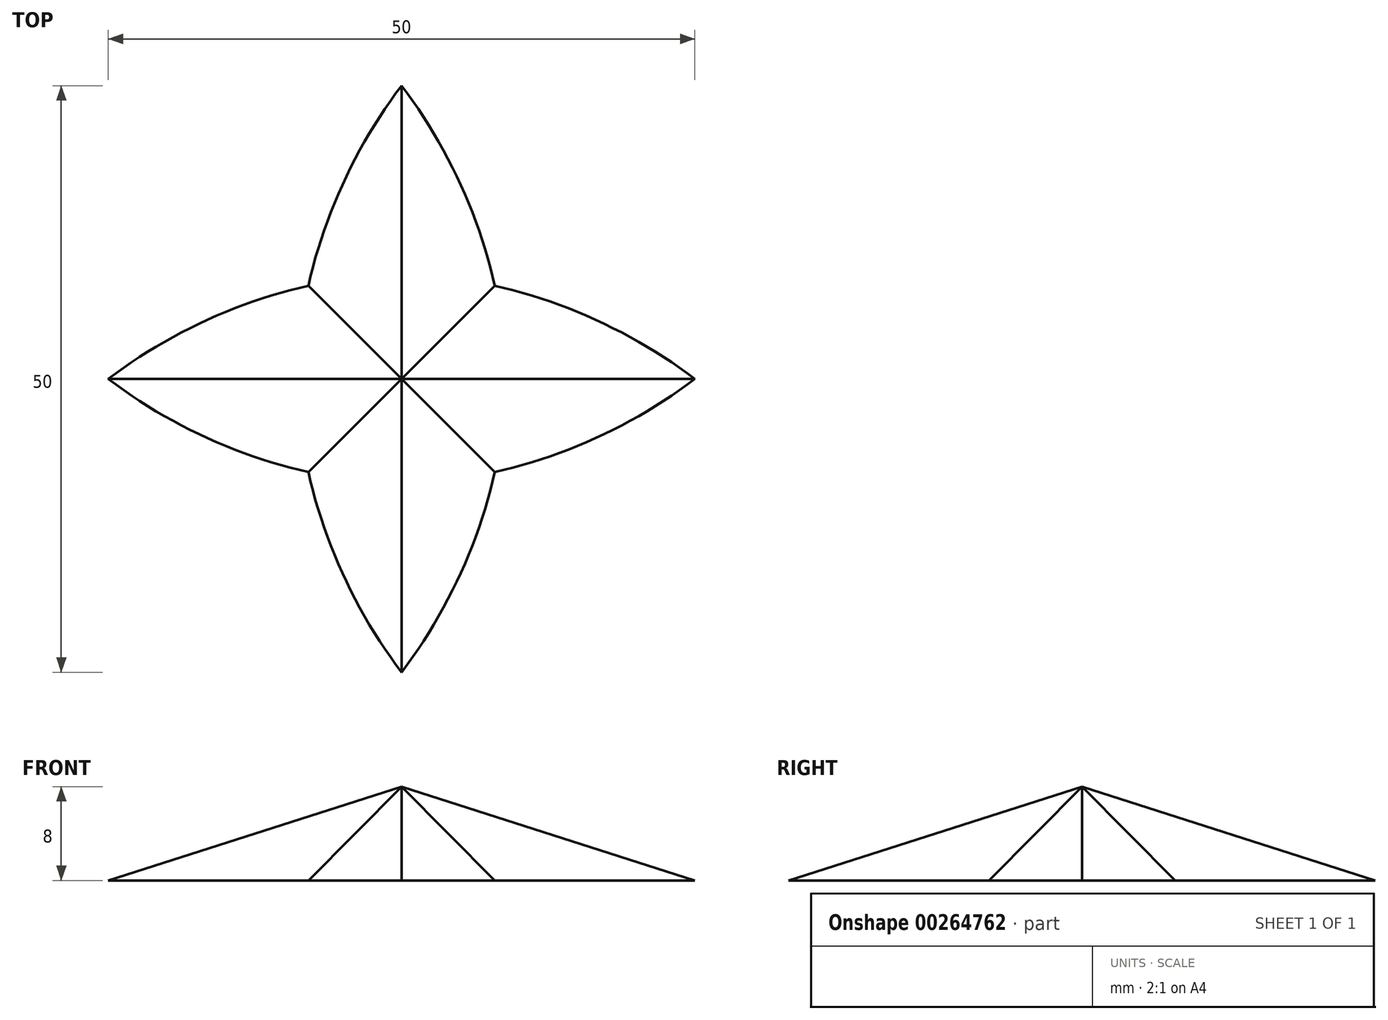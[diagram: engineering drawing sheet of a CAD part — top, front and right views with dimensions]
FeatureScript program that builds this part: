
annotation { "Feature Type Name" : "Feature", "Feature Type Description" : "" }
export const myFeature = defineFeature(function(context is Context, id is Id, definition is map)
    precondition{}
    {
        {
            var Q0;
            Q0=qCreatedBy(makeId("Top.planeOp"),FACE);
            var sketch = newSketch(context, id + "F0", { "sketchPlane" : qUnion([Q0])});
            skLineSegment(sketch, "E0", {"start": v(0, 25.42) * mm, "end": v(0, -24.58) * mm, "construction": true});
            skSolve(sketch);
        }
        {
            var Q0;
            Q0=qCreatedBy(makeId("Top.planeOp"),FACE);
            var sketch = newSketch(context, id + "F1", { "sketchPlane" : qUnion([Q0])});
            skFitSpline(sketch, "E1", {"points": [v(0, 25) * mm, v(-7.94, 7.94) * mm], "startDerivative": vector(-11.26, -14.75) * mm, "endDerivative": vector(-3.95, -18.2) * mm});
            skLineSegment(sketch, "E2", {"start": v(-7.94, 7.94) * mm, "end": v(0, 0) * mm, "construction": true});
            skFitSpline(sketch, "E3.MirrorCS", {"points": [v(0, 25) * mm, v(7.94, 7.94) * mm], "startDerivative": vector(11.26, -14.75) * mm, "endDerivative": vector(3.95, -18.2) * mm});
            skLineSegment(sketch, "E4.MirrorCS", {"start": v(7.94, 7.94) * mm, "end": v(0, 0) * mm, "construction": true});
            skFitSpline(sketch, "E5.MirrorCS", {"points": [v(-25, 0) * mm, v(-7.94, 7.94) * mm], "startDerivative": vector(14.75, 11.26) * mm, "endDerivative": vector(18.2, 3.95) * mm});
            skFitSpline(sketch, "E6.MirrorCS", {"points": [v(-25, 0) * mm, v(-7.94, -7.94) * mm], "startDerivative": vector(14.75, -11.26) * mm, "endDerivative": vector(18.2, -3.95) * mm});
            skFitSpline(sketch, "E7.MirrorCS", {"points": [v(25, 0) * mm, v(7.94, 7.94) * mm], "startDerivative": vector(-14.75, 11.26) * mm, "endDerivative": vector(-18.2, 3.95) * mm});
            skFitSpline(sketch, "E8.MirrorCS", {"points": [v(25, 0) * mm, v(7.94, -7.94) * mm], "startDerivative": vector(-14.75, -11.26) * mm, "endDerivative": vector(-18.2, -3.95) * mm});
            skFitSpline(sketch, "E9.MirrorCS", {"points": [v(0, -25) * mm, v(7.94, -7.94) * mm], "startDerivative": vector(11.26, 14.75) * mm, "endDerivative": vector(3.95, 18.2) * mm});
            skFitSpline(sketch, "E10.MirrorCS", {"points": [v(0, -25) * mm, v(-7.94, -7.94) * mm], "startDerivative": vector(-11.26, 14.75) * mm, "endDerivative": vector(-3.95, 18.2) * mm});
            skLineSegment(sketch, "E11", {"start": v(0, 25) * mm, "end": v(0, -25) * mm, "construction": true});
            skSolve(sketch);
        }
        {
            var Q0;
            Q0=qCreatedBy(makeId("Top.planeOp"),FACE);
            cPlane(context, id + "F2", {"entities" : qUnion([Q0]), "cplaneType" : CPlaneType.OFFSET, "offset" : 8 * mm, "width" : 150 * mm, "height" : 150 * mm});
        }
        {
            var Q0;
            Q0=qCreatedBy(id+"F2.planeOp",FACE);
            var sketch = newSketch(context, id + "F3", { "sketchPlane" : qUnion([Q0])});
            skPoint(sketch, "E12", {"position": v(0, 0) * mm});
            skSolve(sketch);
        }
        {
            var Q0;
            Q0=makeQuery(id+"F1.imprint","IMPRINT",FACE,{"disambiguationData":[TD([[makeQuery(id+"F1.imprint","IMPRINT",EDGE,{"derivedFrom":sQuery(id+"F1.wireOp",EDGE,"E1")}),1.0]])]});
            var Q1;
            Q1=sQuery(id+"F3.wireOp",VERTEX,"E12");
            loft(context, id + "F4", {"sheetProfilesArray" : [{ "sheetProfileEntities" : qUnion([Q0]) }, { "sheetProfileEntities" : qUnion([Q1]) }]});
        }
    });
